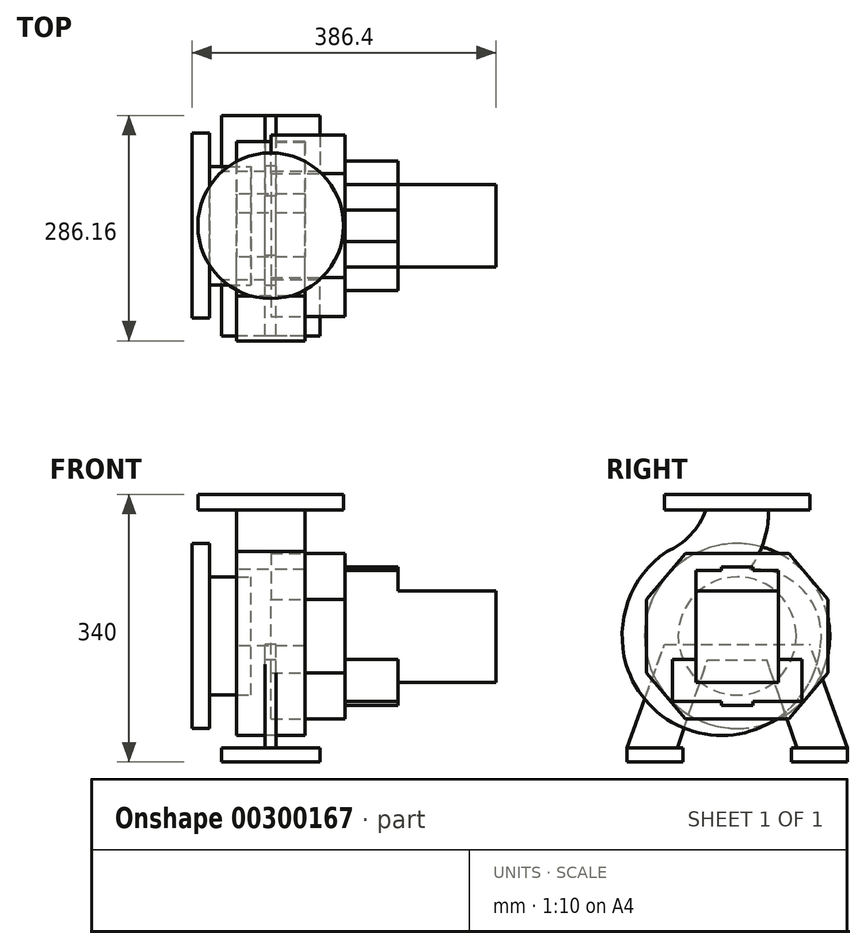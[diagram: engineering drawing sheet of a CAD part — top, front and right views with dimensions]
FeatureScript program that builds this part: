
annotation { "Feature Type Name" : "Feature", "Feature Type Description" : "" }
export const myFeature = defineFeature(function(context is Context, id is Id, definition is map)
    precondition{}
    {
        {
            var Q0;
            Q0=qCreatedBy(makeId("Front.planeOp"),FACE);
            var sketch = newSketch(context, id + "F0", { "sketchPlane" : qUnion([Q0])});
            skLineSegment(sketch, "E0.bottom", {"start": v(-25, 0) * mm, "end": v(-100, 0) * mm});
            skLineSegment(sketch, "E0.right", {"start": v(-100, 0) * mm, "end": v(-100, 117.5) * mm});
            skLineSegment(sketch, "E1.0", {"start": v(-78, 0) * mm, "end": v(-78, 117.5) * mm});
            skLineSegment(sketch, "E2.0", {"start": v(-25, 75) * mm, "end": v(-78, 75) * mm});
            skLineSegment(sketch, "E3.0", {"start": v(-25, 0) * mm, "end": v(-25, 75) * mm});
            skLineSegment(sketch, "E4.trimOffspring", {"start": v(-78, 117.5) * mm, "end": v(-100, 117.5) * mm});
            skPoint(sketch, "E0.top.end.orphan", {"position": v(-100, 180) * mm});
            skSolve(sketch);
        }
        {
            var Q0;
            Q0 = qSketchRegion(id + "F0", true);
            var Q1;
            Q1=sQuery(id+"F0.wireOp",EDGE,"E0.bottom");
            revolve(context, id + "F1", {"entities" : qUnion([Q0]), "axis" : qUnion([Q1]), "revolveType" : RevolveType.FULL});
        }
        {
            var Q0;
            Q0=qCreatedBy(makeId("Front.planeOp"),FACE);
            var sketch = newSketch(context, id + "F2", { "sketchPlane" : qUnion([Q0])});
            skLineSegment(sketch, "E5.bottom", {"start": v(0, 160) * mm, "end": v(-92.5, 160) * mm});
            skLineSegment(sketch, "E5.top", {"start": v(0, 180) * mm, "end": v(-92.5, 180) * mm});
            skLineSegment(sketch, "E5.left", {"start": v(0, 160) * mm, "end": v(0, 180) * mm});
            skLineSegment(sketch, "E5.right", {"start": v(-92.5, 160) * mm, "end": v(-92.5, 180) * mm});
            skSolve(sketch);
        }
        {
            var Q0;
            Q0 = qSketchRegion(id + "F2", true);
            var Q1;
            Q1=sQuery(id+"F2.wireOp",EDGE,"E5.left");
            revolve(context, id + "F3", {"entities" : qUnion([Q0]), "axis" : qUnion([Q1]), "revolveType" : RevolveType.FULL});
        }
        {
            var Q0;
            Q0=qCreatedBy(makeId("Right.planeOp"),FACE);
            var sketch = newSketch(context, id + "F4", { "sketchPlane" : qUnion([Q0])});
            skLineSegment(sketch, "E6.bottom", {"start": v(-140, -142) * mm, "end": v(-76, -142) * mm});
            skLineSegment(sketch, "E6.top", {"start": v(-92.16, -10.55) * mm, "end": v(92.16, -10.55) * mm});
            skLineSegment(sketch, "E7", {"start": v(140, -142) * mm, "end": v(92.16, -10.55) * mm});
            skLineSegment(sketch, "E8", {"start": v(-140, -142) * mm, "end": v(-92.16, -10.55) * mm});
            skLineSegment(sketch, "E9", {"start": v(76, -142) * mm, "end": v(37.62, -30.55) * mm});
            skLineSegment(sketch, "E10", {"start": v(-76, -142) * mm, "end": v(-37.62, -30.55) * mm});
            skLineSegment(sketch, "E11.trimOffspring", {"start": v(-37.62, -30.55) * mm, "end": v(37.62, -30.55) * mm});
            skLineSegment(sketch, "E12.trimOffspring", {"start": v(76, -142) * mm, "end": v(140, -142) * mm});
            skSolve(sketch);
        }
        {
            var Q0;
            Q0=makeQuery(id+"F4.imprint","IMPRINT",FACE,{"disambiguationData":[TD([[makeQuery(id+"F4.imprint","IMPRINT",EDGE,{"derivedFrom":sQuery(id+"F4.wireOp",EDGE,"E6.bottom")}),1.0]])]});
            extrude(context, id + "F5", {"entities" : qUnion([Q0]), "endBound" : BoundingType.SYMMETRIC, "depth" : 14 * mm});
        }
        {
            var Q0;
            Q0=qCreatedBy(makeId("Right.planeOp"),FACE);
            var sketch = newSketch(context, id + "F6", { "sketchPlane" : qUnion([Q0])});
            skLineSegment(sketch, "E13.bottom", {"start": v(140, -142) * mm, "end": v(68.8, -142) * mm});
            skLineSegment(sketch, "E13.top", {"start": v(140, -160) * mm, "end": v(68.8, -160) * mm});
            skLineSegment(sketch, "E13.left", {"start": v(140, -142) * mm, "end": v(140, -160) * mm});
            skLineSegment(sketch, "E13.right", {"start": v(68.8, -142) * mm, "end": v(68.8, -160) * mm});
            skSolve(sketch);
        }
        {
            var Q0;
            Q0 = qSketchRegion(id + "F6", true);
            extrude(context, id + "F7", {"entities" : qUnion([Q0]), "operationType" : NewBodyOperationType.ADD, "endBound" : BoundingType.SYMMETRIC, "depth" : 125 * mm});
        }
        {
            var Q0;
            Q0=qCreatedBy(makeId("Right.planeOp"),FACE);
            var sketch = newSketch(context, id + "F8", { "sketchPlane" : qUnion([Q0])});
            skLineSegment(sketch, "E14.bottom", {"start": v(-140, -142) * mm, "end": v(-68.8, -142) * mm});
            skLineSegment(sketch, "E14.top", {"start": v(-140, -160) * mm, "end": v(-68.8, -160) * mm});
            skLineSegment(sketch, "E14.left", {"start": v(-140, -142) * mm, "end": v(-140, -160) * mm});
            skLineSegment(sketch, "E14.right", {"start": v(-68.8, -142) * mm, "end": v(-68.8, -160) * mm});
            skSolve(sketch);
        }
        {
            var Q0;
            Q0 = qSketchRegion(id + "F8", true);
            extrude(context, id + "F9", {"entities" : qUnion([Q0]), "operationType" : NewBodyOperationType.ADD, "endBound" : BoundingType.SYMMETRIC, "depth" : 125 * mm});
        }
        {
            var Q0;
            Q0=qCreatedBy(makeId("Right.planeOp"),FACE);
            var sketch = newSketch(context, id + "F10", { "sketchPlane" : qUnion([Q0])});
            skArc(sketch, "E15", {"start": v(105.83, -12.37) * mm, "mid": v(84.15, 57.64) * mm, "end": v(16, 84.62) * mm});
            skLineSegment(sketch, "E16.bottom", {"start": v(40, 160) * mm, "end": v(-40, 160) * mm});
            skArc(sketch, "E17", {"start": v(16, 84.62) * mm, "mid": v(33.86, 120.45) * mm, "end": v(40, 160) * mm});
            skArc(sketch, "E18", {"start": v(-89.47, 107.44) * mm, "mid": v(-59.1, 128.42) * mm, "end": v(-40, 160) * mm});
            skArc(sketch, "E19.trimOffspring", {"start": v(-89.47, 107.44) * mm, "mid": v(-138.5, 43.98) * mm, "end": v(-141.03, -36.18) * mm});
            skArc(sketch, "E20.trimOffspring", {"start": v(-141.03, -36.18) * mm, "mid": v(-7.8, -125.8) * mm, "end": v(105.83, -12.37) * mm});
            skPoint(sketch, "E16.top.start.orphan", {"position": v(40, 60) * mm});
            skSolve(sketch);
        }
        {
            var Q0;
            Q0 = qSketchRegion(id + "F10", true);
            extrude(context, id + "F11", {"entities" : qUnion([Q0]), "endBound" : BoundingType.SYMMETRIC, "depth" : 86.87 * mm});
        }
        {
            var Q0;
            Q0=qCreatedBy(makeId("Right.planeOp"),FACE);
            cPlane(context, id + "F12", {"entities" : qUnion([Q0]), "cplaneType" : CPlaneType.OFFSET, "offset" : 94.1 * mm, "width" : 150 * mm, "height" : 150 * mm});
        }
        {
            var Q0;
            Q0=qCreatedBy(id+"F12.planeOp",FACE);
            var sketch = newSketch(context, id + "F13", { "sketchPlane" : qUnion([Q0])});
            skLineSegment(sketch, "E21.top", {"start": v(66, 105) * mm, "end": v(0, 105) * mm});
            skLineSegment(sketch, "E21.left", {"start": v(115, 0) * mm, "end": v(115, 46.6) * mm});
            skLineSegment(sketch, "E22", {"start": v(66, 105) * mm, "end": v(115, 46.6) * mm});
            skPoint(sketch, "E23.orphan", {"position": v(115, 105) * mm});
            skPoint(sketch, "E21.right.end.orphan", {"position": v(-115, 105) * mm});
            skPoint(sketch, "E24.orphan", {"position": v(115, -105) * mm});
            skLineSegment(sketch, "E25.MirrorCS", {"start": v(-66, 105) * mm, "end": v(0, 105) * mm});
            skLineSegment(sketch, "E26.MirrorCS", {"start": v(-66, 105) * mm, "end": v(-115, 46.6) * mm});
            skLineSegment(sketch, "E27.MirrorCS", {"start": v(-115, 0) * mm, "end": v(-115, 46.6) * mm});
            skLineSegment(sketch, "E28.MirrorCS", {"start": v(115, 0) * mm, "end": v(115, -46.6) * mm});
            skLineSegment(sketch, "E29.MirrorCS", {"start": v(66, -105) * mm, "end": v(115, -46.6) * mm});
            skLineSegment(sketch, "E30.MirrorCS", {"start": v(66, -105) * mm, "end": v(0, -105) * mm});
            skLineSegment(sketch, "E31.MirrorCS", {"start": v(-66, -105) * mm, "end": v(0, -105) * mm});
            skLineSegment(sketch, "E32.MirrorCS", {"start": v(-66, -105) * mm, "end": v(-115, -46.6) * mm});
            skLineSegment(sketch, "E33.MirrorCS", {"start": v(-115, 0) * mm, "end": v(-115, -46.6) * mm});
            skSolve(sketch);
        }
        {
            var Q0;
            Q0 = qSketchRegion(id + "F13", true);
            extrude(context, id + "F14", {"entities" : qUnion([Q0]), "oppositeDirection" : true, "depth" : 94 * mm});
        }
        {
            var Q0;
            Q0=qCreatedBy(id+"F12.planeOp",FACE);
            var sketch = newSketch(context, id + "F15", { "sketchPlane" : qUnion([Q0])});
            skLineSegment(sketch, "E34.top", {"start": v(-20, 88) * mm, "end": v(20, 88) * mm});
            skLineSegment(sketch, "E34.left", {"start": v(-52.5, -30) * mm, "end": v(-52.5, 88) * mm});
            skLineSegment(sketch, "E34.right", {"start": v(52.5, -30) * mm, "end": v(52.5, 88) * mm});
            skLineSegment(sketch, "E35.0", {"start": v(-52.5, 83.5) * mm, "end": v(-20, 83.5) * mm});
            skLineSegment(sketch, "E36.0", {"start": v(20, -88) * mm, "end": v(20, -83) * mm});
            skLineSegment(sketch, "E37.0", {"start": v(-20, -88) * mm, "end": v(-20, -83) * mm});
            skLineSegment(sketch, "E38.bottom", {"start": v(-82, -30) * mm, "end": v(-52.5, -30) * mm});
            skLineSegment(sketch, "E38.top", {"start": v(-82, -83) * mm, "end": v(-20, -83) * mm});
            skLineSegment(sketch, "E38.left", {"start": v(-82, -30) * mm, "end": v(-82, -83) * mm});
            skLineSegment(sketch, "E38.right", {"start": v(82, -30) * mm, "end": v(82, -83) * mm});
            skLineSegment(sketch, "E39.0", {"start": v(-20, -88) * mm, "end": v(20, -88) * mm});
            skLineSegment(sketch, "E40.trimOffspring", {"start": v(20, -83) * mm, "end": v(82, -83) * mm});
            skLineSegment(sketch, "E41.trimOffspring", {"start": v(52.5, -30) * mm, "end": v(82, -30) * mm});
            skLineSegment(sketch, "E42.trimOffspring", {"start": v(20, 83.5) * mm, "end": v(52.5, 83.5) * mm});
            skLineSegment(sketch, "E43.trimOffspring", {"start": v(20, 83.5) * mm, "end": v(20, 88) * mm});
            skLineSegment(sketch, "E44.trimOffspring", {"start": v(-20, 83.5) * mm, "end": v(-20, 88) * mm});
            skSolve(sketch);
        }
        {
            var Q0;
            Q0 = qSketchRegion(id + "F15", true);
            extrude(context, id + "F16", {"entities" : qUnion([Q0]), "operationType" : NewBodyOperationType.ADD, "depth" : 67.5 * mm});
        }
        {
            var Q0;
            Q0=qCreatedBy(id+"F12.planeOp",FACE);
            cPlane(context, id + "F17", {"entities" : qUnion([Q0]), "cplaneType" : CPlaneType.OFFSET, "offset" : 67.5 * mm, "width" : 150 * mm, "height" : 150 * mm});
        }
        {
            var Q0;
            Q0=qCreatedBy(id+"F17.planeOp",FACE);
            var sketch = newSketch(context, id + "F18", { "sketchPlane" : qUnion([Q0])});
            skLineSegment(sketch, "E45.bottom", {"start": v(-52.5, -59) * mm, "end": v(52.5, -59) * mm});
            skLineSegment(sketch, "E45.top", {"start": v(-52.5, 57.5) * mm, "end": v(52.5, 57.5) * mm});
            skLineSegment(sketch, "E45.left", {"start": v(-52.5, -59) * mm, "end": v(-52.5, 57.5) * mm});
            skLineSegment(sketch, "E45.right", {"start": v(52.5, -59) * mm, "end": v(52.5, 57.5) * mm});
            skSolve(sketch);
        }
        {
            var Q0;
            Q0 = qSketchRegion(id + "F18", true);
            extrude(context, id + "F19", {"entities" : qUnion([Q0]), "operationType" : NewBodyOperationType.ADD, "depth" : 124.8 * mm});
        }
    });
